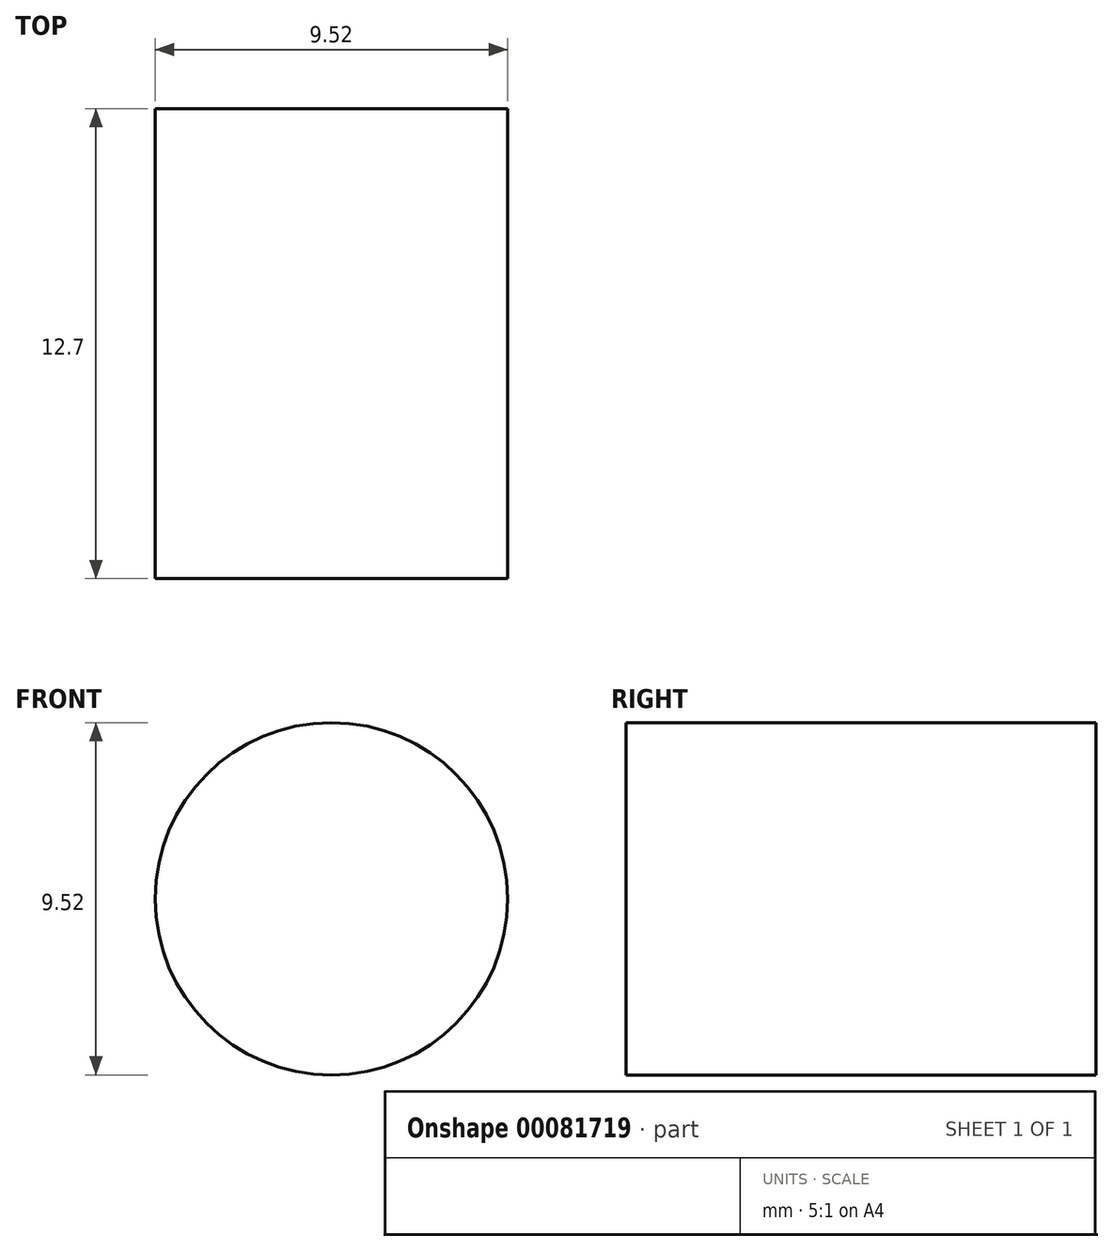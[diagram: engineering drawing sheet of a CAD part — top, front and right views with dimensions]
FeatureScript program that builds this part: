
annotation { "Feature Type Name" : "Feature", "Feature Type Description" : "" }
export const myFeature = defineFeature(function(context is Context, id is Id, definition is map)
    precondition{}
    {
        {
            var Q0;
            Q0=qCreatedBy(makeId("Front.planeOp"),FACE);
            var sketch = newSketch(context, id + "F0", { "sketchPlane" : qUnion([Q0])});
            skCircle(sketch, "E0", {"center": v(0, 0) * mm, "radius": 4.76 * mm});
            skSolve(sketch);
        }
        {
            var Q0;
            Q0=makeQuery(id+"F0.imprint","IMPRINT",FACE,{"disambiguationData":[TD([[makeQuery(id+"F0.imprint","IMPRINT",EDGE,{"derivedFrom":sQuery(id+"F0.wireOp",EDGE,"E0")}),1.0]])]});
            extrude(context, id + "F1", {"entities" : qUnion([Q0]), "depth" : 12.7 * mm});
        }
    });
